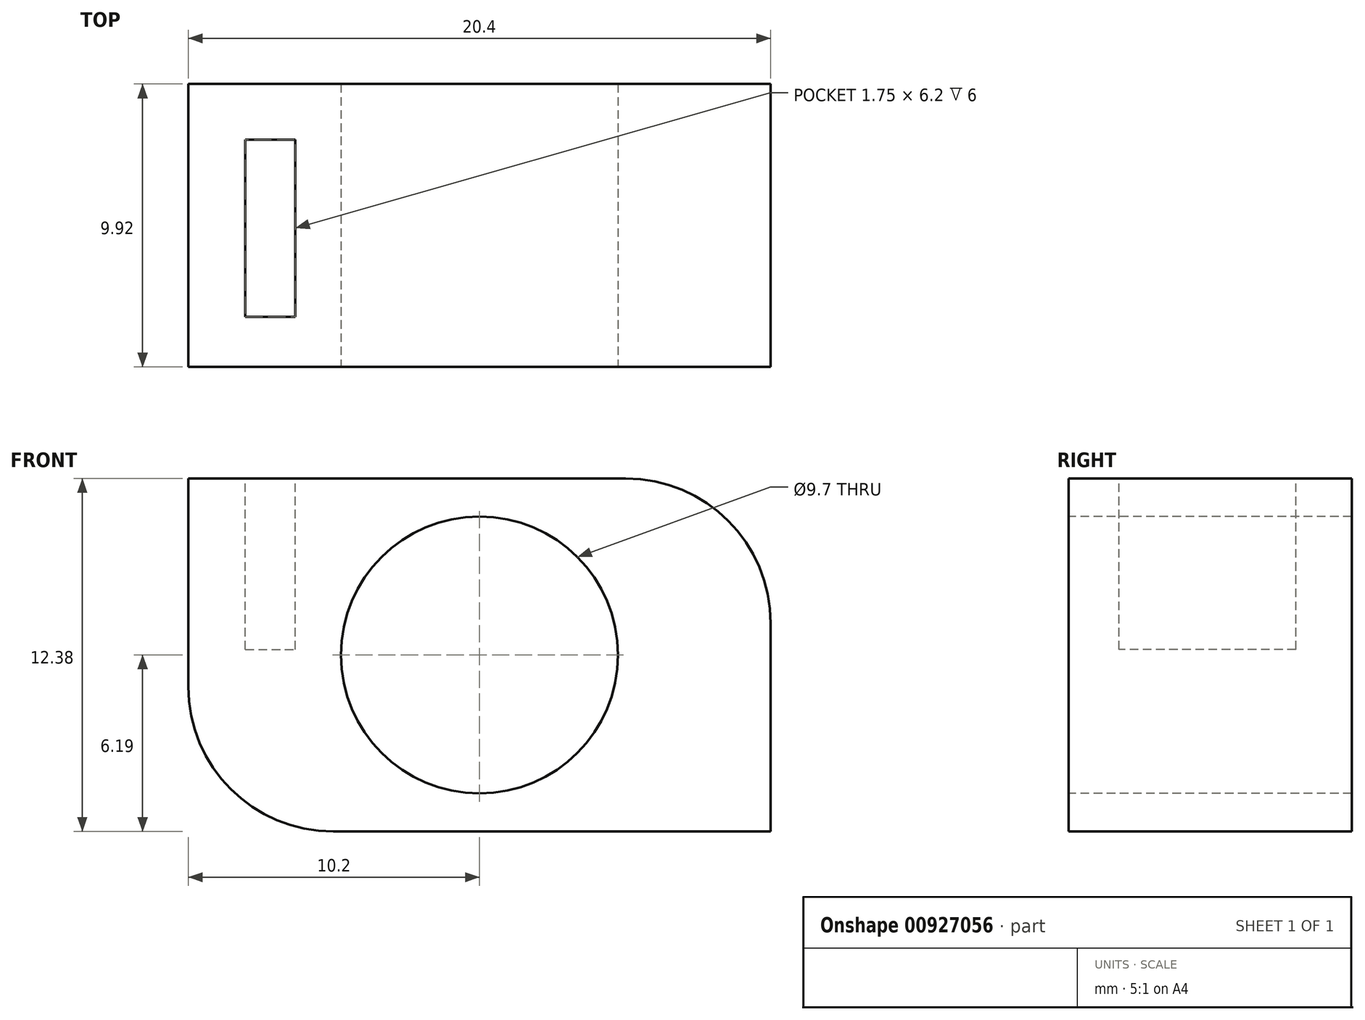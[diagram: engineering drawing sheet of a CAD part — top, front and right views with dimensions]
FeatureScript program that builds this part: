
annotation { "Feature Type Name" : "Feature", "Feature Type Description" : "" }
export const myFeature = defineFeature(function(context is Context, id is Id, definition is map)
    precondition{}
    {
        {
            var Q0;
            Q0=qCreatedBy(makeId("Front.planeOp"),FACE);
            var sketch = newSketch(context, id + "F0", { "sketchPlane" : qUnion([Q0])});
            skLineSegment(sketch, "E0.bottom", {"start": v(10.2, 6.2) * mm, "end": v(-10.2, 6.2) * mm});
            skLineSegment(sketch, "E0.top", {"start": v(10.2, -6.2) * mm, "end": v(-10.2, -6.2) * mm});
            skLineSegment(sketch, "E0.left", {"start": v(10.2, 6.2) * mm, "end": v(10.2, -6.2) * mm});
            skLineSegment(sketch, "E0.right", {"start": v(-10.2, 6.2) * mm, "end": v(-10.2, -6.2) * mm});
            skPoint(sketch, "E0.middle", {"position": v(0, 0) * mm});
            skSolve(sketch);
        }
        {
            var Q0;
            Q0 = qSketchRegion(id + "F0", true);
            extrude(context, id + "F1", {"entities" : qUnion([Q0]), "depth" : 9.92 * mm, "offsetDistance" : 25.4 * mm});
        }
        {
            var Q0;
            Q0=makeQuery(id+"F1.opExtrude","CAP_FACE",FACE,{"disambiguationData":[OSD([sQuery(id+"F0.wireOp",EDGE,"E0.bottom"),sQuery(id+"F0.wireOp",EDGE,"E0.top"),sQuery(id+"F0.wireOp",EDGE,"E0.left"),sQuery(id+"F0.wireOp",EDGE,"E0.right")])],"isStart":false});
            var sketch = newSketch(context, id + "F2", { "sketchPlane" : qUnion([Q0])});
            skPoint(sketch, "E1", {"position": v(0, 0) * mm});
            skSolve(sketch);
        }
        {
            var Q0;
            Q0=sQuery(id+"F2.wireOp",VERTEX,"E1");
            var Q1;
            Q1=makeQuery(id+"F1.opExtrude","SWEPT_BODY",BODY,{"disambiguationData":[OSD([sQuery(id+"F0.wireOp",EDGE,"E0.bottom"),sQuery(id+"F0.wireOp",EDGE,"E0.top"),sQuery(id+"F0.wireOp",EDGE,"E0.left"),sQuery(id+"F0.wireOp",EDGE,"E0.right")])]});
            hole(context, id + "F3", {"style" : HoleStyle.SIMPLE, "endStyle" : HoleEndStyle.THROUGH, "holeDiameter" : 9.7 * mm, "majorDiameter" : 6.35 * mm, "isTappedThrough" : true, "tappedDepth" : 12.7 * mm, "tapClearance" : 3, "locations" : qUnion([Q0]), "scope" : qUnion([Q1])});
        }
        {
            var Q0;
            Q0=makeQuery(id+"F1.opExtrude","SWEPT_EDGE",EDGE,{"disambiguationData":[OSD([sQuery(id+"F0.wireOp",EDGE,"E0.bottom"),sQuery(id+"F0.wireOp",EDGE,"E0.left")])]});
            fillet(context, id + "F4", {"entities" : qUnion([Q0]), "radius" : 5.08 * mm, "tangentPropagation" : true, "allowEdgeOverflow" : false});
        }
        {
            var Q0;
            Q0=makeQuery(id+"F1.opExtrude","SWEPT_FACE",FACE,{"disambiguationData":[OSD([sQuery(id+"F0.wireOp",EDGE,"E0.bottom")])]});
            var sketch = newSketch(context, id + "F5", { "sketchPlane" : qUnion([Q0])});
            skLineSegment(sketch, "E2.bottom", {"start": v(-8.2, -1.96) * mm, "end": v(-6.45, -1.96) * mm});
            skLineSegment(sketch, "E2.top", {"start": v(-8.2, -8.16) * mm, "end": v(-6.45, -8.16) * mm});
            skLineSegment(sketch, "E2.left", {"start": v(-8.2, -1.96) * mm, "end": v(-8.2, -8.16) * mm});
            skLineSegment(sketch, "E2.right", {"start": v(-6.45, -1.96) * mm, "end": v(-6.45, -8.16) * mm});
            skSolve(sketch);
        }
        {
            var Q0;
            Q0 = qSketchRegion(id + "F5", true);
            extrude(context, id + "F6", {"entities" : qUnion([Q0]), "operationType" : NewBodyOperationType.REMOVE, "oppositeDirection" : true, "depth" : 6 * mm, "offsetDistance" : 25.4 * mm});
        }
        {
            var Q0;
            Q0=makeQuery(id+"F1.opExtrude","SWEPT_EDGE",EDGE,{"disambiguationData":[OSD([sQuery(id+"F0.wireOp",EDGE,"E0.top"),sQuery(id+"F0.wireOp",EDGE,"E0.right")])]});
            fillet(context, id + "F7", {"entities" : qUnion([Q0]), "radius" : 5.08 * mm, "tangentPropagation" : true, "allowEdgeOverflow" : false});
        }
    });
